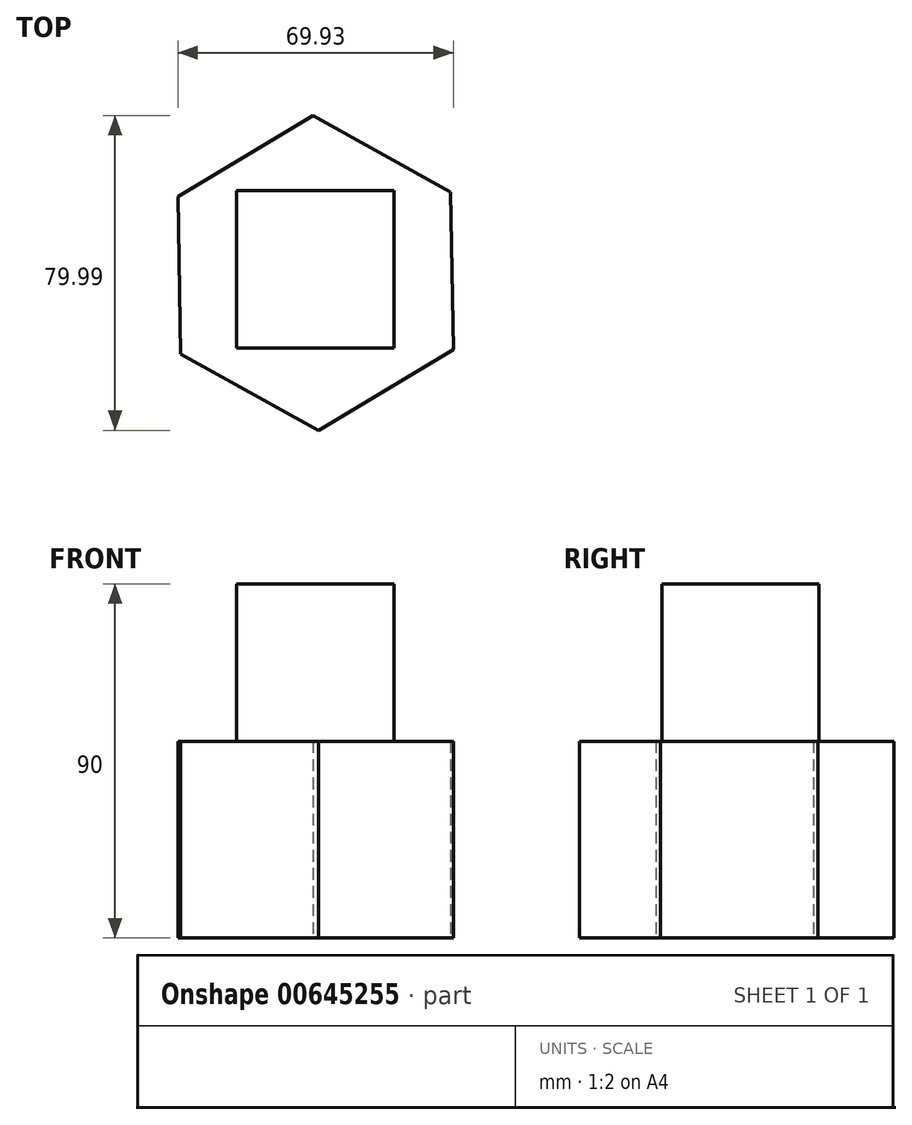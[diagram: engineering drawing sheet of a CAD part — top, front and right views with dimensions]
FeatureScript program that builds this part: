
annotation { "Feature Type Name" : "Feature", "Feature Type Description" : "" }
export const myFeature = defineFeature(function(context is Context, id is Id, definition is map)
    precondition{}
    {
        {
            var Q0;
            Q0=qCreatedBy(makeId("Top.planeOp"),FACE);
            var sketch = newSketch(context, id + "F0", { "sketchPlane" : qUnion([Q0])});
            skCircle(sketch, "E0.cCircle", {"center": v(-27.83, 39.33) * mm, "radius": 34.64 * mm, "construction": true});
            skLineSegment(sketch, "E0.0", {"start": v(-27.17, -0.67) * mm, "end": v(-62.14, 18.76) * mm});
            skLineSegment(sketch, "E0.1", {"start": v(-62.14, 18.76) * mm, "end": v(-62.8, 58.75) * mm});
            skLineSegment(sketch, "E0.2", {"start": v(-62.8, 58.75) * mm, "end": v(-28.5, 79.32) * mm});
            skLineSegment(sketch, "E0.3", {"start": v(-28.5, 79.32) * mm, "end": v(6.47, 59.9) * mm});
            skLineSegment(sketch, "E0.4", {"start": v(6.47, 59.9) * mm, "end": v(7.13, 19.9) * mm});
            skLineSegment(sketch, "E0.5", {"start": v(7.13, 19.9) * mm, "end": v(-27.17, -0.67) * mm});
            skPoint(sketch, "E0.0.midPoint", {"position": v(-44.66, 9.05) * mm});
            skSolve(sketch);
        }
        {
            var Q0;
            Q0 = qSketchRegion(id + "F0", true);
            extrude(context, id + "F1", {"entities" : qUnion([Q0]), "depth" : 50 * mm, "offsetDistance" : 25.4 * mm});
        }
        {
            var Q0;
            Q0=makeQuery(id+"F1.opExtrude","CAP_FACE",FACE,{"disambiguationData":[OSD([sQuery(id+"F0.wireOp",EDGE,"E0.0"),sQuery(id+"F0.wireOp",EDGE,"E0.1"),sQuery(id+"F0.wireOp",EDGE,"E0.2"),sQuery(id+"F0.wireOp",EDGE,"E0.3"),sQuery(id+"F0.wireOp",EDGE,"E0.4"),sQuery(id+"F0.wireOp",EDGE,"E0.5")])],"isStart":false});
            var sketch = newSketch(context, id + "F2", { "sketchPlane" : qUnion([Q0])});
            skLineSegment(sketch, "E1.bottom", {"start": v(-47.98, 60.27) * mm, "end": v(-7.98, 60.27) * mm});
            skLineSegment(sketch, "E1.top", {"start": v(-47.98, 20.27) * mm, "end": v(-7.98, 20.27) * mm});
            skLineSegment(sketch, "E1.left", {"start": v(-47.98, 60.27) * mm, "end": v(-47.98, 20.27) * mm});
            skLineSegment(sketch, "E1.right", {"start": v(-7.98, 60.27) * mm, "end": v(-7.98, 20.27) * mm});
            skSolve(sketch);
        }
        {
            var Q0;
            Q0 = qSketchRegion(id + "F2", true);
            extrude(context, id + "F3", {"entities" : qUnion([Q0]), "operationType" : NewBodyOperationType.ADD, "depth" : 40 * mm, "offsetDistance" : 25.4 * mm});
        }
    });
